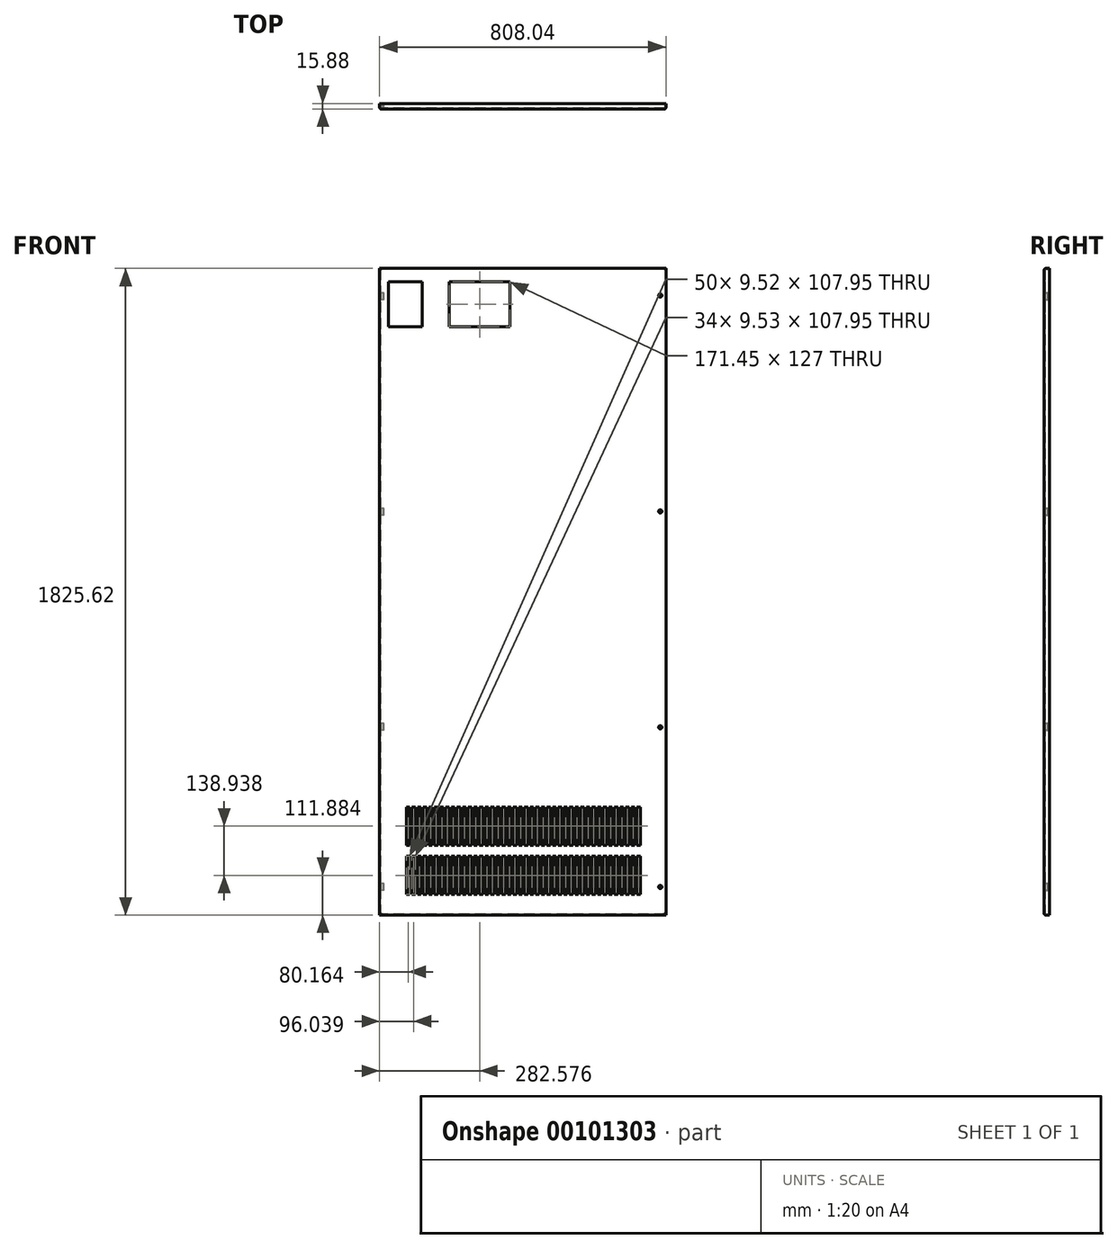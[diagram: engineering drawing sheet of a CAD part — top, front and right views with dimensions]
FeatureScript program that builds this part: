
annotation { "Feature Type Name" : "Feature", "Feature Type Description" : "" }
export const myFeature = defineFeature(function(context is Context, id is Id, definition is map)
    precondition{}
    {
        {
            var Q0;
            Q0=qCreatedBy(makeId("Front.planeOp"),FACE);
            var sketch = newSketch(context, id + "F0", { "sketchPlane" : qUnion([Q0])});
            skLineSegment(sketch, "E0.bottom", {"start": v(404.02, 912.81) * mm, "end": v(-404.02, 912.81) * mm});
            skLineSegment(sketch, "E0.top", {"start": v(404.02, -912.81) * mm, "end": v(-404.02, -912.81) * mm});
            skLineSegment(sketch, "E0.left", {"start": v(404.02, 912.81) * mm, "end": v(404.02, -912.81) * mm});
            skLineSegment(sketch, "E0.right", {"start": v(-404.02, 912.81) * mm, "end": v(-404.02, -912.81) * mm});
            skPoint(sketch, "E0.middle", {"position": v(0, 0) * mm});
            skSolve(sketch);
        }
        {
            var Q0;
            Q0=makeQuery(id+"F0.imprint","IMPRINT",FACE,{"disambiguationData":[TD([[makeQuery(id+"F0.imprint","IMPRINT",EDGE,{"derivedFrom":sQuery(id+"F0.wireOp",EDGE,"E0.bottom")}),1.0]])]});
            var Q1;
            Q1=qSketchRegion(id+"F0",true);
            extrude(context, id + "F1", {"entities" : qUnion([Q0, Q1]), "endBound" : BoundingType.SYMMETRIC, "depth" : 15.88 * mm});
        }
        {
            var Q0;
            Q0=makeQuery(id+"F1.opExtrude","CAP_FACE",FACE,{"disambiguationData":[OSD([sQuery(id+"F0.wireOp",EDGE,"E0.bottom"),sQuery(id+"F0.wireOp",EDGE,"E0.top"),sQuery(id+"F0.wireOp",EDGE,"E0.left"),sQuery(id+"F0.wireOp",EDGE,"E0.right")])],"isStart":true});
            shell(context, id + "F2", {"entities" : qUnion([Q0]), "thickness" : 2.66 * mm});
        }
        {
            var Q0;
            Q0=makeQuery(id+"F1.opExtrude","CAP_EDGE",EDGE,{"disambiguationData":[OSD([sQuery(id+"F0.wireOp",EDGE,"E0.bottom")])],"isStart":false});
            var Q1;
            Q1=makeQuery(id+"F1.opExtrude","CAP_EDGE",EDGE,{"disambiguationData":[OSD([sQuery(id+"F0.wireOp",EDGE,"E0.left")])],"isStart":false});
            var Q2;
            Q2=makeQuery(id+"F1.opExtrude","CAP_EDGE",EDGE,{"disambiguationData":[OSD([sQuery(id+"F0.wireOp",EDGE,"E0.right")])],"isStart":false});
            var Q3;
            Q3=makeQuery(id+"F1.opExtrude","CAP_EDGE",EDGE,{"disambiguationData":[OSD([sQuery(id+"F0.wireOp",EDGE,"E0.top")])],"isStart":false});
            fillet(context, id + "F3", {"entities" : qUnion([Q0, Q1, Q2, Q3]), "radius" : 5.08 * mm, "tangentPropagation" : true, "allowEdgeOverflow" : false});
        }
        {
            var Q0;
            Q0=makeQuery(id+"F1.opExtrude","CAP_FACE",FACE,{"disambiguationData":[OSD([sQuery(id+"F0.wireOp",EDGE,"E0.bottom"),sQuery(id+"F0.wireOp",EDGE,"E0.top"),sQuery(id+"F0.wireOp",EDGE,"E0.left"),sQuery(id+"F0.wireOp",EDGE,"E0.right")])],"isStart":false});
            var sketch = newSketch(context, id + "F4", { "sketchPlane" : qUnion([Q0])});
            skLineSegment(sketch, "E1.bottom", {"start": v(-378.62, 874.71) * mm, "end": v(-283.37, 874.71) * mm});
            skLineSegment(sketch, "E1.top", {"start": v(-378.62, 747.71) * mm, "end": v(-283.37, 747.71) * mm});
            skLineSegment(sketch, "E1.left", {"start": v(-378.62, 874.71) * mm, "end": v(-378.62, 747.71) * mm});
            skLineSegment(sketch, "E1.right", {"start": v(-283.37, 874.71) * mm, "end": v(-283.37, 747.71) * mm});
            skCircle(sketch, "E2", {"center": v(388.14, 836.61) * mm, "radius": 4.76 * mm});
            skCircle(sketch, "E3", {"center": v(388.14, -382.59) * mm, "radius": 4.76 * mm});
            skCircle(sketch, "E4", {"center": v(388.14, -833.44) * mm, "radius": 4.76 * mm});
            skLineSegment(sketch, "E5.bottom", {"start": v(322.26, -854.9) * mm, "end": v(331.78, -854.9) * mm});
            skLineSegment(sketch, "E5.top", {"start": v(322.26, -746.95) * mm, "end": v(331.78, -746.95) * mm});
            skLineSegment(sketch, "E5.left", {"start": v(322.26, -854.9) * mm, "end": v(322.26, -746.95) * mm});
            skLineSegment(sketch, "E5.right", {"start": v(331.78, -854.9) * mm, "end": v(331.78, -746.95) * mm});
            skLineSegment(sketch, "E6.1.0.0", {"start": v(315.9, -854.9) * mm, "end": v(315.9, -746.95) * mm});
            skLineSegment(sketch, "E6.1.0.1", {"start": v(306.38, -854.9) * mm, "end": v(306.38, -746.95) * mm});
            skLineSegment(sketch, "E6.1.0.2", {"start": v(306.38, -854.9) * mm, "end": v(315.9, -854.9) * mm});
            skLineSegment(sketch, "E6.1.0.3", {"start": v(306.38, -746.95) * mm, "end": v(315.9, -746.95) * mm});
            skLineSegment(sketch, "E6.2.0.0", {"start": v(300.03, -854.9) * mm, "end": v(300.03, -746.95) * mm});
            skLineSegment(sketch, "E6.2.0.1", {"start": v(290.5, -854.9) * mm, "end": v(290.5, -746.95) * mm});
            skLineSegment(sketch, "E6.2.0.2", {"start": v(290.5, -854.9) * mm, "end": v(300.03, -854.9) * mm});
            skLineSegment(sketch, "E6.2.0.3", {"start": v(290.5, -746.95) * mm, "end": v(300.03, -746.95) * mm});
            skLineSegment(sketch, "E6.3.0.0", {"start": v(284.16, -854.9) * mm, "end": v(284.16, -746.95) * mm});
            skLineSegment(sketch, "E6.3.0.1", {"start": v(274.63, -854.9) * mm, "end": v(274.63, -746.95) * mm});
            skLineSegment(sketch, "E6.3.0.2", {"start": v(274.63, -854.9) * mm, "end": v(284.16, -854.9) * mm});
            skLineSegment(sketch, "E6.3.0.3", {"start": v(274.63, -746.95) * mm, "end": v(284.16, -746.95) * mm});
            skLineSegment(sketch, "E6.4.0.0", {"start": v(268.28, -854.9) * mm, "end": v(268.28, -746.95) * mm});
            skLineSegment(sketch, "E6.4.0.1", {"start": v(258.76, -854.9) * mm, "end": v(258.76, -746.95) * mm});
            skLineSegment(sketch, "E6.4.0.2", {"start": v(258.76, -854.9) * mm, "end": v(268.28, -854.9) * mm});
            skLineSegment(sketch, "E6.4.0.3", {"start": v(258.76, -746.95) * mm, "end": v(268.28, -746.95) * mm});
            skLineSegment(sketch, "E6.5.0.0", {"start": v(252.4, -854.9) * mm, "end": v(252.4, -746.95) * mm});
            skLineSegment(sketch, "E6.5.0.1", {"start": v(242.88, -854.9) * mm, "end": v(242.88, -746.95) * mm});
            skLineSegment(sketch, "E6.5.0.2", {"start": v(242.88, -854.9) * mm, "end": v(252.4, -854.9) * mm});
            skLineSegment(sketch, "E6.5.0.3", {"start": v(242.88, -746.95) * mm, "end": v(252.4, -746.95) * mm});
            skLineSegment(sketch, "E6.6.0.0", {"start": v(236.53, -854.9) * mm, "end": v(236.53, -746.95) * mm});
            skLineSegment(sketch, "E6.6.0.1", {"start": v(227, -854.9) * mm, "end": v(227, -746.95) * mm});
            skLineSegment(sketch, "E6.6.0.2", {"start": v(227, -854.9) * mm, "end": v(236.53, -854.9) * mm});
            skLineSegment(sketch, "E6.6.0.3", {"start": v(227, -746.95) * mm, "end": v(236.53, -746.95) * mm});
            skLineSegment(sketch, "E6.7.0.0", {"start": v(220.66, -854.9) * mm, "end": v(220.66, -746.95) * mm});
            skLineSegment(sketch, "E6.7.0.1", {"start": v(211.13, -854.9) * mm, "end": v(211.13, -746.95) * mm});
            skLineSegment(sketch, "E6.7.0.2", {"start": v(211.13, -854.9) * mm, "end": v(220.66, -854.9) * mm});
            skLineSegment(sketch, "E6.7.0.3", {"start": v(211.13, -746.95) * mm, "end": v(220.66, -746.95) * mm});
            skLineSegment(sketch, "E6.8.0.0", {"start": v(204.78, -854.9) * mm, "end": v(204.78, -746.95) * mm});
            skLineSegment(sketch, "E6.8.0.1", {"start": v(195.26, -854.9) * mm, "end": v(195.26, -746.95) * mm});
            skLineSegment(sketch, "E6.8.0.2", {"start": v(195.26, -854.9) * mm, "end": v(204.78, -854.9) * mm});
            skLineSegment(sketch, "E6.8.0.3", {"start": v(195.26, -746.95) * mm, "end": v(204.78, -746.95) * mm});
            skLineSegment(sketch, "E6.9.0.0", {"start": v(188.9, -854.9) * mm, "end": v(188.9, -746.95) * mm});
            skLineSegment(sketch, "E6.9.0.1", {"start": v(179.38, -854.9) * mm, "end": v(179.38, -746.95) * mm});
            skLineSegment(sketch, "E6.9.0.2", {"start": v(179.38, -854.9) * mm, "end": v(188.9, -854.9) * mm});
            skLineSegment(sketch, "E6.9.0.3", {"start": v(179.38, -746.95) * mm, "end": v(188.9, -746.95) * mm});
            skLineSegment(sketch, "E6.10.0.0", {"start": v(173.03, -854.9) * mm, "end": v(173.03, -746.95) * mm});
            skLineSegment(sketch, "E6.10.0.1", {"start": v(163.5, -854.9) * mm, "end": v(163.5, -746.95) * mm});
            skLineSegment(sketch, "E6.10.0.2", {"start": v(163.5, -854.9) * mm, "end": v(173.03, -854.9) * mm});
            skLineSegment(sketch, "E6.10.0.3", {"start": v(163.5, -746.95) * mm, "end": v(173.03, -746.95) * mm});
            skLineSegment(sketch, "E6.11.0.0", {"start": v(157.16, -854.9) * mm, "end": v(157.16, -746.95) * mm});
            skLineSegment(sketch, "E6.11.0.1", {"start": v(147.63, -854.9) * mm, "end": v(147.63, -746.95) * mm});
            skLineSegment(sketch, "E6.11.0.2", {"start": v(147.63, -854.9) * mm, "end": v(157.16, -854.9) * mm});
            skLineSegment(sketch, "E6.11.0.3", {"start": v(147.63, -746.95) * mm, "end": v(157.16, -746.95) * mm});
            skLineSegment(sketch, "E6.12.0.0", {"start": v(141.28, -854.9) * mm, "end": v(141.28, -746.95) * mm});
            skLineSegment(sketch, "E6.12.0.1", {"start": v(131.76, -854.9) * mm, "end": v(131.76, -746.95) * mm});
            skLineSegment(sketch, "E6.12.0.2", {"start": v(131.76, -854.9) * mm, "end": v(141.28, -854.9) * mm});
            skLineSegment(sketch, "E6.12.0.3", {"start": v(131.76, -746.95) * mm, "end": v(141.28, -746.95) * mm});
            skLineSegment(sketch, "E6.13.0.0", {"start": v(125.4, -854.9) * mm, "end": v(125.4, -746.95) * mm});
            skLineSegment(sketch, "E6.13.0.1", {"start": v(115.88, -854.9) * mm, "end": v(115.88, -746.95) * mm});
            skLineSegment(sketch, "E6.13.0.2", {"start": v(115.88, -854.9) * mm, "end": v(125.4, -854.9) * mm});
            skLineSegment(sketch, "E6.13.0.3", {"start": v(115.88, -746.95) * mm, "end": v(125.4, -746.95) * mm});
            skLineSegment(sketch, "E6.14.0.0", {"start": v(109.53, -854.9) * mm, "end": v(109.53, -746.95) * mm});
            skLineSegment(sketch, "E6.14.0.1", {"start": v(100, -854.9) * mm, "end": v(100, -746.95) * mm});
            skLineSegment(sketch, "E6.14.0.2", {"start": v(100, -854.9) * mm, "end": v(109.53, -854.9) * mm});
            skLineSegment(sketch, "E6.14.0.3", {"start": v(100, -746.95) * mm, "end": v(109.53, -746.95) * mm});
            skLineSegment(sketch, "E6.15.0.0", {"start": v(93.66, -854.9) * mm, "end": v(93.66, -746.95) * mm});
            skLineSegment(sketch, "E6.15.0.1", {"start": v(84.13, -854.9) * mm, "end": v(84.13, -746.95) * mm});
            skLineSegment(sketch, "E6.15.0.2", {"start": v(84.13, -854.9) * mm, "end": v(93.66, -854.9) * mm});
            skLineSegment(sketch, "E6.15.0.3", {"start": v(84.13, -746.95) * mm, "end": v(93.66, -746.95) * mm});
            skLineSegment(sketch, "E6.16.0.0", {"start": v(77.78, -854.9) * mm, "end": v(77.78, -746.95) * mm});
            skLineSegment(sketch, "E6.16.0.1", {"start": v(68.26, -854.9) * mm, "end": v(68.26, -746.95) * mm});
            skLineSegment(sketch, "E6.16.0.2", {"start": v(68.26, -854.9) * mm, "end": v(77.78, -854.9) * mm});
            skLineSegment(sketch, "E6.16.0.3", {"start": v(68.26, -746.95) * mm, "end": v(77.78, -746.95) * mm});
            skLineSegment(sketch, "E6.17.0.0", {"start": v(61.9, -854.9) * mm, "end": v(61.9, -746.95) * mm});
            skLineSegment(sketch, "E6.17.0.1", {"start": v(52.38, -854.9) * mm, "end": v(52.38, -746.95) * mm});
            skLineSegment(sketch, "E6.17.0.2", {"start": v(52.38, -854.9) * mm, "end": v(61.9, -854.9) * mm});
            skLineSegment(sketch, "E6.17.0.3", {"start": v(52.38, -746.95) * mm, "end": v(61.9, -746.95) * mm});
            skLineSegment(sketch, "E6.18.0.0", {"start": v(46.03, -854.9) * mm, "end": v(46.03, -746.95) * mm});
            skLineSegment(sketch, "E6.18.0.1", {"start": v(36.5, -854.9) * mm, "end": v(36.5, -746.95) * mm});
            skLineSegment(sketch, "E6.18.0.2", {"start": v(36.5, -854.9) * mm, "end": v(46.03, -854.9) * mm});
            skLineSegment(sketch, "E6.18.0.3", {"start": v(36.5, -746.95) * mm, "end": v(46.03, -746.95) * mm});
            skLineSegment(sketch, "E6.19.0.0", {"start": v(30.16, -854.9) * mm, "end": v(30.16, -746.95) * mm});
            skLineSegment(sketch, "E6.19.0.1", {"start": v(20.63, -854.9) * mm, "end": v(20.63, -746.95) * mm});
            skLineSegment(sketch, "E6.19.0.2", {"start": v(20.63, -854.9) * mm, "end": v(30.16, -854.9) * mm});
            skLineSegment(sketch, "E6.19.0.3", {"start": v(20.63, -746.95) * mm, "end": v(30.16, -746.95) * mm});
            skLineSegment(sketch, "E6.20.0.0", {"start": v(14.28, -854.9) * mm, "end": v(14.28, -746.95) * mm});
            skLineSegment(sketch, "E6.20.0.1", {"start": v(4.76, -854.9) * mm, "end": v(4.76, -746.95) * mm});
            skLineSegment(sketch, "E6.20.0.2", {"start": v(4.76, -854.9) * mm, "end": v(14.28, -854.9) * mm});
            skLineSegment(sketch, "E6.20.0.3", {"start": v(4.76, -746.95) * mm, "end": v(14.28, -746.95) * mm});
            skLineSegment(sketch, "E6.21.0.0", {"start": v(-1.6, -854.9) * mm, "end": v(-1.6, -746.95) * mm});
            skLineSegment(sketch, "E6.21.0.1", {"start": v(-11.12, -854.9) * mm, "end": v(-11.12, -746.95) * mm});
            skLineSegment(sketch, "E6.21.0.2", {"start": v(-11.12, -854.9) * mm, "end": v(-1.6, -854.9) * mm});
            skLineSegment(sketch, "E6.21.0.3", {"start": v(-11.12, -746.95) * mm, "end": v(-1.6, -746.95) * mm});
            skLineSegment(sketch, "E6.22.0.0", {"start": v(-17.47, -854.9) * mm, "end": v(-17.47, -746.95) * mm});
            skLineSegment(sketch, "E6.22.0.1", {"start": v(-27, -854.9) * mm, "end": v(-27, -746.95) * mm});
            skLineSegment(sketch, "E6.22.0.2", {"start": v(-27, -854.9) * mm, "end": v(-17.47, -854.9) * mm});
            skLineSegment(sketch, "E6.22.0.3", {"start": v(-27, -746.95) * mm, "end": v(-17.47, -746.95) * mm});
            skLineSegment(sketch, "E6.23.0.0", {"start": v(-33.34, -854.9) * mm, "end": v(-33.34, -746.95) * mm});
            skLineSegment(sketch, "E6.23.0.1", {"start": v(-42.87, -854.9) * mm, "end": v(-42.87, -746.95) * mm});
            skLineSegment(sketch, "E6.23.0.2", {"start": v(-42.87, -854.9) * mm, "end": v(-33.34, -854.9) * mm});
            skLineSegment(sketch, "E6.23.0.3", {"start": v(-42.87, -746.95) * mm, "end": v(-33.34, -746.95) * mm});
            skLineSegment(sketch, "E6.24.0.0", {"start": v(-49.22, -854.9) * mm, "end": v(-49.22, -746.95) * mm});
            skLineSegment(sketch, "E6.24.0.1", {"start": v(-58.74, -854.9) * mm, "end": v(-58.74, -746.95) * mm});
            skLineSegment(sketch, "E6.24.0.2", {"start": v(-58.74, -854.9) * mm, "end": v(-49.22, -854.9) * mm});
            skLineSegment(sketch, "E6.24.0.3", {"start": v(-58.74, -746.95) * mm, "end": v(-49.22, -746.95) * mm});
            skLineSegment(sketch, "E6.25.0.0", {"start": v(-65.1, -854.9) * mm, "end": v(-65.1, -746.95) * mm});
            skLineSegment(sketch, "E6.25.0.1", {"start": v(-74.62, -854.9) * mm, "end": v(-74.62, -746.95) * mm});
            skLineSegment(sketch, "E6.25.0.2", {"start": v(-74.62, -854.9) * mm, "end": v(-65.1, -854.9) * mm});
            skLineSegment(sketch, "E6.25.0.3", {"start": v(-74.62, -746.95) * mm, "end": v(-65.1, -746.95) * mm});
            skLineSegment(sketch, "E6.26.0.0", {"start": v(-80.97, -854.9) * mm, "end": v(-80.97, -746.95) * mm});
            skLineSegment(sketch, "E6.26.0.1", {"start": v(-90.5, -854.9) * mm, "end": v(-90.5, -746.95) * mm});
            skLineSegment(sketch, "E6.26.0.2", {"start": v(-90.5, -854.9) * mm, "end": v(-80.97, -854.9) * mm});
            skLineSegment(sketch, "E6.26.0.3", {"start": v(-90.5, -746.95) * mm, "end": v(-80.97, -746.95) * mm});
            skLineSegment(sketch, "E6.27.0.0", {"start": v(-96.84, -854.9) * mm, "end": v(-96.84, -746.95) * mm});
            skLineSegment(sketch, "E6.27.0.1", {"start": v(-106.37, -854.9) * mm, "end": v(-106.37, -746.95) * mm});
            skLineSegment(sketch, "E6.27.0.2", {"start": v(-106.37, -854.9) * mm, "end": v(-96.84, -854.9) * mm});
            skLineSegment(sketch, "E6.27.0.3", {"start": v(-106.37, -746.95) * mm, "end": v(-96.84, -746.95) * mm});
            skLineSegment(sketch, "E6.28.0.0", {"start": v(-112.72, -854.9) * mm, "end": v(-112.72, -746.95) * mm});
            skLineSegment(sketch, "E6.28.0.1", {"start": v(-122.24, -854.9) * mm, "end": v(-122.24, -746.95) * mm});
            skLineSegment(sketch, "E6.28.0.2", {"start": v(-122.24, -854.9) * mm, "end": v(-112.72, -854.9) * mm});
            skLineSegment(sketch, "E6.28.0.3", {"start": v(-122.24, -746.95) * mm, "end": v(-112.72, -746.95) * mm});
            skLineSegment(sketch, "E6.29.0.0", {"start": v(-128.6, -854.9) * mm, "end": v(-128.6, -746.95) * mm});
            skLineSegment(sketch, "E6.29.0.1", {"start": v(-138.12, -854.9) * mm, "end": v(-138.12, -746.95) * mm});
            skLineSegment(sketch, "E6.29.0.2", {"start": v(-138.12, -854.9) * mm, "end": v(-128.6, -854.9) * mm});
            skLineSegment(sketch, "E6.29.0.3", {"start": v(-138.12, -746.95) * mm, "end": v(-128.6, -746.95) * mm});
            skLineSegment(sketch, "E6.30.0.0", {"start": v(-144.47, -854.9) * mm, "end": v(-144.47, -746.95) * mm});
            skLineSegment(sketch, "E6.30.0.1", {"start": v(-154, -854.9) * mm, "end": v(-154, -746.95) * mm});
            skLineSegment(sketch, "E6.30.0.2", {"start": v(-154, -854.9) * mm, "end": v(-144.47, -854.9) * mm});
            skLineSegment(sketch, "E6.30.0.3", {"start": v(-154, -746.95) * mm, "end": v(-144.47, -746.95) * mm});
            skLineSegment(sketch, "E6.31.0.0", {"start": v(-160.34, -854.9) * mm, "end": v(-160.34, -746.95) * mm});
            skLineSegment(sketch, "E6.31.0.1", {"start": v(-169.87, -854.9) * mm, "end": v(-169.87, -746.95) * mm});
            skLineSegment(sketch, "E6.31.0.2", {"start": v(-169.87, -854.9) * mm, "end": v(-160.34, -854.9) * mm});
            skLineSegment(sketch, "E6.31.0.3", {"start": v(-169.87, -746.95) * mm, "end": v(-160.34, -746.95) * mm});
            skLineSegment(sketch, "E6.32.0.0", {"start": v(-176.22, -854.9) * mm, "end": v(-176.22, -746.95) * mm});
            skLineSegment(sketch, "E6.32.0.1", {"start": v(-185.74, -854.9) * mm, "end": v(-185.74, -746.95) * mm});
            skLineSegment(sketch, "E6.32.0.2", {"start": v(-185.74, -854.9) * mm, "end": v(-176.22, -854.9) * mm});
            skLineSegment(sketch, "E6.32.0.3", {"start": v(-185.74, -746.95) * mm, "end": v(-176.22, -746.95) * mm});
            skLineSegment(sketch, "E6.33.0.0", {"start": v(-192.1, -854.9) * mm, "end": v(-192.1, -746.95) * mm});
            skLineSegment(sketch, "E6.33.0.1", {"start": v(-201.62, -854.9) * mm, "end": v(-201.62, -746.95) * mm});
            skLineSegment(sketch, "E6.33.0.2", {"start": v(-201.62, -854.9) * mm, "end": v(-192.1, -854.9) * mm});
            skLineSegment(sketch, "E6.33.0.3", {"start": v(-201.62, -746.95) * mm, "end": v(-192.1, -746.95) * mm});
            skLineSegment(sketch, "E6.direction1", {"start": v(331.78, -854.9) * mm, "end": v(315.9, -854.9) * mm, "construction": true});
            skLineSegment(sketch, "E6.direction2", {"start": v(331.78, -854.9) * mm, "end": v(331.78, -715.96) * mm, "construction": true});
            skLineSegment(sketch, "E7.0.34.0", {"start": v(-207.97, -854.9) * mm, "end": v(-207.97, -746.95) * mm});
            skLineSegment(sketch, "E7.3.34.0", {"start": v(-217.5, -854.9) * mm, "end": v(-217.5, -746.95) * mm});
            skLineSegment(sketch, "E7.6.34.0", {"start": v(-217.5, -854.9) * mm, "end": v(-207.97, -854.9) * mm});
            skLineSegment(sketch, "E7.9.34.0", {"start": v(-217.5, -746.95) * mm, "end": v(-207.97, -746.95) * mm});
            skLineSegment(sketch, "E7.0.35.0", {"start": v(-223.84, -854.9) * mm, "end": v(-223.84, -746.95) * mm});
            skLineSegment(sketch, "E7.3.35.0", {"start": v(-233.37, -854.9) * mm, "end": v(-233.37, -746.95) * mm});
            skLineSegment(sketch, "E7.6.35.0", {"start": v(-233.37, -854.9) * mm, "end": v(-223.84, -854.9) * mm});
            skLineSegment(sketch, "E7.9.35.0", {"start": v(-233.37, -746.95) * mm, "end": v(-223.84, -746.95) * mm});
            skLineSegment(sketch, "E7.0.36.0", {"start": v(-239.72, -854.9) * mm, "end": v(-239.72, -746.95) * mm});
            skLineSegment(sketch, "E7.3.36.0", {"start": v(-249.24, -854.9) * mm, "end": v(-249.24, -746.95) * mm});
            skLineSegment(sketch, "E7.6.36.0", {"start": v(-249.24, -854.9) * mm, "end": v(-239.72, -854.9) * mm});
            skLineSegment(sketch, "E7.9.36.0", {"start": v(-249.24, -746.95) * mm, "end": v(-239.72, -746.95) * mm});
            skLineSegment(sketch, "E7.0.37.0", {"start": v(-255.6, -854.9) * mm, "end": v(-255.6, -746.95) * mm});
            skLineSegment(sketch, "E7.3.37.0", {"start": v(-265.12, -854.9) * mm, "end": v(-265.12, -746.95) * mm});
            skLineSegment(sketch, "E7.6.37.0", {"start": v(-265.12, -854.9) * mm, "end": v(-255.6, -854.9) * mm});
            skLineSegment(sketch, "E7.9.37.0", {"start": v(-265.12, -746.95) * mm, "end": v(-255.6, -746.95) * mm});
            skLineSegment(sketch, "E7.0.38.0", {"start": v(-271.47, -854.9) * mm, "end": v(-271.47, -746.95) * mm});
            skLineSegment(sketch, "E7.3.38.0", {"start": v(-281, -854.9) * mm, "end": v(-281, -746.95) * mm});
            skLineSegment(sketch, "E7.6.38.0", {"start": v(-281, -854.9) * mm, "end": v(-271.47, -854.9) * mm});
            skLineSegment(sketch, "E7.9.38.0", {"start": v(-281, -746.95) * mm, "end": v(-271.47, -746.95) * mm});
            skLineSegment(sketch, "E7.0.39.0", {"start": v(-287.34, -854.9) * mm, "end": v(-287.34, -746.95) * mm});
            skLineSegment(sketch, "E7.3.39.0", {"start": v(-296.87, -854.9) * mm, "end": v(-296.87, -746.95) * mm});
            skLineSegment(sketch, "E7.6.39.0", {"start": v(-296.87, -854.9) * mm, "end": v(-287.34, -854.9) * mm});
            skLineSegment(sketch, "E7.9.39.0", {"start": v(-296.87, -746.95) * mm, "end": v(-287.34, -746.95) * mm});
            skLineSegment(sketch, "E7.0.40.0", {"start": v(-303.22, -854.9) * mm, "end": v(-303.22, -746.95) * mm});
            skLineSegment(sketch, "E7.3.40.0", {"start": v(-312.74, -854.9) * mm, "end": v(-312.74, -746.95) * mm});
            skLineSegment(sketch, "E7.6.40.0", {"start": v(-312.74, -854.9) * mm, "end": v(-303.22, -854.9) * mm});
            skLineSegment(sketch, "E7.9.40.0", {"start": v(-312.74, -746.95) * mm, "end": v(-303.22, -746.95) * mm});
            skLineSegment(sketch, "E7.0.41.0", {"start": v(-319.1, -854.9) * mm, "end": v(-319.1, -746.95) * mm});
            skLineSegment(sketch, "E7.3.41.0", {"start": v(-328.62, -854.9) * mm, "end": v(-328.62, -746.95) * mm});
            skLineSegment(sketch, "E7.6.41.0", {"start": v(-328.62, -854.9) * mm, "end": v(-319.1, -854.9) * mm});
            skLineSegment(sketch, "E7.9.41.0", {"start": v(-328.62, -746.95) * mm, "end": v(-319.1, -746.95) * mm});
            skLineSegment(sketch, "E8.direction1", {"start": v(-281, -854.9) * mm, "end": v(-259.44, -854.9) * mm, "construction": true});
            skLineSegment(sketch, "E9.0.0.1", {"start": v(331.78, -715.96) * mm, "end": v(331.78, -608.01) * mm});
            skLineSegment(sketch, "E9.3.0.1", {"start": v(322.26, -715.96) * mm, "end": v(322.26, -608.01) * mm});
            skLineSegment(sketch, "E9.6.0.1", {"start": v(322.26, -715.96) * mm, "end": v(331.78, -715.96) * mm});
            skLineSegment(sketch, "E9.9.0.1", {"start": v(322.26, -608.01) * mm, "end": v(331.78, -608.01) * mm});
            skLineSegment(sketch, "E9.0.1.1", {"start": v(315.9, -715.96) * mm, "end": v(315.9, -608.01) * mm});
            skLineSegment(sketch, "E9.3.1.1", {"start": v(306.38, -715.96) * mm, "end": v(306.38, -608.01) * mm});
            skLineSegment(sketch, "E9.6.1.1", {"start": v(306.38, -715.96) * mm, "end": v(315.9, -715.96) * mm});
            skLineSegment(sketch, "E9.9.1.1", {"start": v(306.38, -608.01) * mm, "end": v(315.9, -608.01) * mm});
            skLineSegment(sketch, "E9.0.2.1", {"start": v(300.03, -715.96) * mm, "end": v(300.03, -608.01) * mm});
            skLineSegment(sketch, "E9.3.2.1", {"start": v(290.5, -715.96) * mm, "end": v(290.5, -608.01) * mm});
            skLineSegment(sketch, "E9.6.2.1", {"start": v(290.5, -715.96) * mm, "end": v(300.03, -715.96) * mm});
            skLineSegment(sketch, "E9.9.2.1", {"start": v(290.5, -608.01) * mm, "end": v(300.03, -608.01) * mm});
            skLineSegment(sketch, "E9.0.3.1", {"start": v(284.16, -715.96) * mm, "end": v(284.16, -608.01) * mm});
            skLineSegment(sketch, "E9.3.3.1", {"start": v(274.63, -715.96) * mm, "end": v(274.63, -608.01) * mm});
            skLineSegment(sketch, "E9.6.3.1", {"start": v(274.63, -715.96) * mm, "end": v(284.16, -715.96) * mm});
            skLineSegment(sketch, "E9.9.3.1", {"start": v(274.63, -608.01) * mm, "end": v(284.16, -608.01) * mm});
            skLineSegment(sketch, "E9.0.4.1", {"start": v(268.28, -715.96) * mm, "end": v(268.28, -608.01) * mm});
            skLineSegment(sketch, "E9.3.4.1", {"start": v(258.76, -715.96) * mm, "end": v(258.76, -608.01) * mm});
            skLineSegment(sketch, "E9.6.4.1", {"start": v(258.76, -715.96) * mm, "end": v(268.28, -715.96) * mm});
            skLineSegment(sketch, "E9.9.4.1", {"start": v(258.76, -608.01) * mm, "end": v(268.28, -608.01) * mm});
            skLineSegment(sketch, "E9.0.5.1", {"start": v(252.4, -715.96) * mm, "end": v(252.4, -608.01) * mm});
            skLineSegment(sketch, "E9.3.5.1", {"start": v(242.88, -715.96) * mm, "end": v(242.88, -608.01) * mm});
            skLineSegment(sketch, "E9.6.5.1", {"start": v(242.88, -715.96) * mm, "end": v(252.4, -715.96) * mm});
            skLineSegment(sketch, "E9.9.5.1", {"start": v(242.88, -608.01) * mm, "end": v(252.4, -608.01) * mm});
            skLineSegment(sketch, "E9.0.6.1", {"start": v(236.53, -715.96) * mm, "end": v(236.53, -608.01) * mm});
            skLineSegment(sketch, "E9.3.6.1", {"start": v(227, -715.96) * mm, "end": v(227, -608.01) * mm});
            skLineSegment(sketch, "E9.6.6.1", {"start": v(227, -715.96) * mm, "end": v(236.53, -715.96) * mm});
            skLineSegment(sketch, "E9.9.6.1", {"start": v(227, -608.01) * mm, "end": v(236.53, -608.01) * mm});
            skLineSegment(sketch, "E9.0.7.1", {"start": v(220.66, -715.96) * mm, "end": v(220.66, -608.01) * mm});
            skLineSegment(sketch, "E9.3.7.1", {"start": v(211.13, -715.96) * mm, "end": v(211.13, -608.01) * mm});
            skLineSegment(sketch, "E9.6.7.1", {"start": v(211.13, -715.96) * mm, "end": v(220.66, -715.96) * mm});
            skLineSegment(sketch, "E9.9.7.1", {"start": v(211.13, -608.01) * mm, "end": v(220.66, -608.01) * mm});
            skLineSegment(sketch, "E9.0.8.1", {"start": v(204.78, -715.96) * mm, "end": v(204.78, -608.01) * mm});
            skLineSegment(sketch, "E9.3.8.1", {"start": v(195.26, -715.96) * mm, "end": v(195.26, -608.01) * mm});
            skLineSegment(sketch, "E9.6.8.1", {"start": v(195.26, -715.96) * mm, "end": v(204.78, -715.96) * mm});
            skLineSegment(sketch, "E9.9.8.1", {"start": v(195.26, -608.01) * mm, "end": v(204.78, -608.01) * mm});
            skLineSegment(sketch, "E9.0.9.1", {"start": v(188.9, -715.96) * mm, "end": v(188.9, -608.01) * mm});
            skLineSegment(sketch, "E9.3.9.1", {"start": v(179.38, -715.96) * mm, "end": v(179.38, -608.01) * mm});
            skLineSegment(sketch, "E9.6.9.1", {"start": v(179.38, -715.96) * mm, "end": v(188.9, -715.96) * mm});
            skLineSegment(sketch, "E9.9.9.1", {"start": v(179.38, -608.01) * mm, "end": v(188.9, -608.01) * mm});
            skLineSegment(sketch, "E9.0.10.1", {"start": v(173.03, -715.96) * mm, "end": v(173.03, -608.01) * mm});
            skLineSegment(sketch, "E9.3.10.1", {"start": v(163.5, -715.96) * mm, "end": v(163.5, -608.01) * mm});
            skLineSegment(sketch, "E9.6.10.1", {"start": v(163.5, -715.96) * mm, "end": v(173.03, -715.96) * mm});
            skLineSegment(sketch, "E9.9.10.1", {"start": v(163.5, -608.01) * mm, "end": v(173.03, -608.01) * mm});
            skLineSegment(sketch, "E9.0.11.1", {"start": v(157.16, -715.96) * mm, "end": v(157.16, -608.01) * mm});
            skLineSegment(sketch, "E9.3.11.1", {"start": v(147.63, -715.96) * mm, "end": v(147.63, -608.01) * mm});
            skLineSegment(sketch, "E9.6.11.1", {"start": v(147.63, -715.96) * mm, "end": v(157.16, -715.96) * mm});
            skLineSegment(sketch, "E9.9.11.1", {"start": v(147.63, -608.01) * mm, "end": v(157.16, -608.01) * mm});
            skLineSegment(sketch, "E9.0.12.1", {"start": v(141.28, -715.96) * mm, "end": v(141.28, -608.01) * mm});
            skLineSegment(sketch, "E9.3.12.1", {"start": v(131.76, -715.96) * mm, "end": v(131.76, -608.01) * mm});
            skLineSegment(sketch, "E9.6.12.1", {"start": v(131.76, -715.96) * mm, "end": v(141.28, -715.96) * mm});
            skLineSegment(sketch, "E9.9.12.1", {"start": v(131.76, -608.01) * mm, "end": v(141.28, -608.01) * mm});
            skLineSegment(sketch, "E9.0.13.1", {"start": v(125.4, -715.96) * mm, "end": v(125.4, -608.01) * mm});
            skLineSegment(sketch, "E9.3.13.1", {"start": v(115.88, -715.96) * mm, "end": v(115.88, -608.01) * mm});
            skLineSegment(sketch, "E9.6.13.1", {"start": v(115.88, -715.96) * mm, "end": v(125.4, -715.96) * mm});
            skLineSegment(sketch, "E9.9.13.1", {"start": v(115.88, -608.01) * mm, "end": v(125.4, -608.01) * mm});
            skLineSegment(sketch, "E9.0.14.1", {"start": v(109.53, -715.96) * mm, "end": v(109.53, -608.01) * mm});
            skLineSegment(sketch, "E9.3.14.1", {"start": v(100, -715.96) * mm, "end": v(100, -608.01) * mm});
            skLineSegment(sketch, "E9.6.14.1", {"start": v(100, -715.96) * mm, "end": v(109.53, -715.96) * mm});
            skLineSegment(sketch, "E9.9.14.1", {"start": v(100, -608.01) * mm, "end": v(109.53, -608.01) * mm});
            skLineSegment(sketch, "E9.0.15.1", {"start": v(93.66, -715.96) * mm, "end": v(93.66, -608.01) * mm});
            skLineSegment(sketch, "E9.3.15.1", {"start": v(84.13, -715.96) * mm, "end": v(84.13, -608.01) * mm});
            skLineSegment(sketch, "E9.6.15.1", {"start": v(84.13, -715.96) * mm, "end": v(93.66, -715.96) * mm});
            skLineSegment(sketch, "E9.9.15.1", {"start": v(84.13, -608.01) * mm, "end": v(93.66, -608.01) * mm});
            skLineSegment(sketch, "E9.0.16.1", {"start": v(77.78, -715.96) * mm, "end": v(77.78, -608.01) * mm});
            skLineSegment(sketch, "E9.3.16.1", {"start": v(68.26, -715.96) * mm, "end": v(68.26, -608.01) * mm});
            skLineSegment(sketch, "E9.6.16.1", {"start": v(68.26, -715.96) * mm, "end": v(77.78, -715.96) * mm});
            skLineSegment(sketch, "E9.9.16.1", {"start": v(68.26, -608.01) * mm, "end": v(77.78, -608.01) * mm});
            skLineSegment(sketch, "E9.0.17.1", {"start": v(61.9, -715.96) * mm, "end": v(61.9, -608.01) * mm});
            skLineSegment(sketch, "E9.3.17.1", {"start": v(52.38, -715.96) * mm, "end": v(52.38, -608.01) * mm});
            skLineSegment(sketch, "E9.6.17.1", {"start": v(52.38, -715.96) * mm, "end": v(61.9, -715.96) * mm});
            skLineSegment(sketch, "E9.9.17.1", {"start": v(52.38, -608.01) * mm, "end": v(61.9, -608.01) * mm});
            skLineSegment(sketch, "E9.0.18.1", {"start": v(46.03, -715.96) * mm, "end": v(46.03, -608.01) * mm});
            skLineSegment(sketch, "E9.3.18.1", {"start": v(36.5, -715.96) * mm, "end": v(36.5, -608.01) * mm});
            skLineSegment(sketch, "E9.6.18.1", {"start": v(36.5, -715.96) * mm, "end": v(46.03, -715.96) * mm});
            skLineSegment(sketch, "E9.9.18.1", {"start": v(36.5, -608.01) * mm, "end": v(46.03, -608.01) * mm});
            skLineSegment(sketch, "E9.0.19.1", {"start": v(30.16, -715.96) * mm, "end": v(30.16, -608.01) * mm});
            skLineSegment(sketch, "E9.3.19.1", {"start": v(20.63, -715.96) * mm, "end": v(20.63, -608.01) * mm});
            skLineSegment(sketch, "E9.6.19.1", {"start": v(20.63, -715.96) * mm, "end": v(30.16, -715.96) * mm});
            skLineSegment(sketch, "E9.9.19.1", {"start": v(20.63, -608.01) * mm, "end": v(30.16, -608.01) * mm});
            skLineSegment(sketch, "E9.0.20.1", {"start": v(14.28, -715.96) * mm, "end": v(14.28, -608.01) * mm});
            skLineSegment(sketch, "E9.3.20.1", {"start": v(4.76, -715.96) * mm, "end": v(4.76, -608.01) * mm});
            skLineSegment(sketch, "E9.6.20.1", {"start": v(4.76, -715.96) * mm, "end": v(14.28, -715.96) * mm});
            skLineSegment(sketch, "E9.9.20.1", {"start": v(4.76, -608.01) * mm, "end": v(14.28, -608.01) * mm});
            skLineSegment(sketch, "E9.0.21.1", {"start": v(-1.6, -715.96) * mm, "end": v(-1.6, -608.01) * mm});
            skLineSegment(sketch, "E9.3.21.1", {"start": v(-11.12, -715.96) * mm, "end": v(-11.12, -608.01) * mm});
            skLineSegment(sketch, "E9.6.21.1", {"start": v(-11.12, -715.96) * mm, "end": v(-1.6, -715.96) * mm});
            skLineSegment(sketch, "E9.9.21.1", {"start": v(-11.12, -608.01) * mm, "end": v(-1.6, -608.01) * mm});
            skLineSegment(sketch, "E9.0.22.1", {"start": v(-17.47, -715.96) * mm, "end": v(-17.47, -608.01) * mm});
            skLineSegment(sketch, "E9.3.22.1", {"start": v(-27, -715.96) * mm, "end": v(-27, -608.01) * mm});
            skLineSegment(sketch, "E9.6.22.1", {"start": v(-27, -715.96) * mm, "end": v(-17.47, -715.96) * mm});
            skLineSegment(sketch, "E9.9.22.1", {"start": v(-27, -608.01) * mm, "end": v(-17.47, -608.01) * mm});
            skLineSegment(sketch, "E9.0.23.1", {"start": v(-33.34, -715.96) * mm, "end": v(-33.34, -608.01) * mm});
            skLineSegment(sketch, "E9.3.23.1", {"start": v(-42.87, -715.96) * mm, "end": v(-42.87, -608.01) * mm});
            skLineSegment(sketch, "E9.6.23.1", {"start": v(-42.87, -715.96) * mm, "end": v(-33.34, -715.96) * mm});
            skLineSegment(sketch, "E9.9.23.1", {"start": v(-42.87, -608.01) * mm, "end": v(-33.34, -608.01) * mm});
            skLineSegment(sketch, "E9.0.24.1", {"start": v(-49.22, -715.96) * mm, "end": v(-49.22, -608.01) * mm});
            skLineSegment(sketch, "E9.3.24.1", {"start": v(-58.74, -715.96) * mm, "end": v(-58.74, -608.01) * mm});
            skLineSegment(sketch, "E9.6.24.1", {"start": v(-58.74, -715.96) * mm, "end": v(-49.22, -715.96) * mm});
            skLineSegment(sketch, "E9.9.24.1", {"start": v(-58.74, -608.01) * mm, "end": v(-49.22, -608.01) * mm});
            skLineSegment(sketch, "E9.0.25.1", {"start": v(-65.1, -715.96) * mm, "end": v(-65.1, -608.01) * mm});
            skLineSegment(sketch, "E9.3.25.1", {"start": v(-74.62, -715.96) * mm, "end": v(-74.62, -608.01) * mm});
            skLineSegment(sketch, "E9.6.25.1", {"start": v(-74.62, -715.96) * mm, "end": v(-65.1, -715.96) * mm});
            skLineSegment(sketch, "E9.9.25.1", {"start": v(-74.62, -608.01) * mm, "end": v(-65.1, -608.01) * mm});
            skLineSegment(sketch, "E9.0.26.1", {"start": v(-80.97, -715.96) * mm, "end": v(-80.97, -608.01) * mm});
            skLineSegment(sketch, "E9.3.26.1", {"start": v(-90.5, -715.96) * mm, "end": v(-90.5, -608.01) * mm});
            skLineSegment(sketch, "E9.6.26.1", {"start": v(-90.5, -715.96) * mm, "end": v(-80.97, -715.96) * mm});
            skLineSegment(sketch, "E9.9.26.1", {"start": v(-90.5, -608.01) * mm, "end": v(-80.97, -608.01) * mm});
            skLineSegment(sketch, "E9.0.27.1", {"start": v(-96.84, -715.96) * mm, "end": v(-96.84, -608.01) * mm});
            skLineSegment(sketch, "E9.3.27.1", {"start": v(-106.37, -715.96) * mm, "end": v(-106.37, -608.01) * mm});
            skLineSegment(sketch, "E9.6.27.1", {"start": v(-106.37, -715.96) * mm, "end": v(-96.84, -715.96) * mm});
            skLineSegment(sketch, "E9.9.27.1", {"start": v(-106.37, -608.01) * mm, "end": v(-96.84, -608.01) * mm});
            skLineSegment(sketch, "E9.0.28.1", {"start": v(-112.72, -715.96) * mm, "end": v(-112.72, -608.01) * mm});
            skLineSegment(sketch, "E9.3.28.1", {"start": v(-122.24, -715.96) * mm, "end": v(-122.24, -608.01) * mm});
            skLineSegment(sketch, "E9.6.28.1", {"start": v(-122.24, -715.96) * mm, "end": v(-112.72, -715.96) * mm});
            skLineSegment(sketch, "E9.9.28.1", {"start": v(-122.24, -608.01) * mm, "end": v(-112.72, -608.01) * mm});
            skLineSegment(sketch, "E9.0.29.1", {"start": v(-128.6, -715.96) * mm, "end": v(-128.6, -608.01) * mm});
            skLineSegment(sketch, "E9.3.29.1", {"start": v(-138.12, -715.96) * mm, "end": v(-138.12, -608.01) * mm});
            skLineSegment(sketch, "E9.6.29.1", {"start": v(-138.12, -715.96) * mm, "end": v(-128.6, -715.96) * mm});
            skLineSegment(sketch, "E9.9.29.1", {"start": v(-138.12, -608.01) * mm, "end": v(-128.6, -608.01) * mm});
            skLineSegment(sketch, "E9.0.30.1", {"start": v(-144.47, -715.96) * mm, "end": v(-144.47, -608.01) * mm});
            skLineSegment(sketch, "E9.3.30.1", {"start": v(-154, -715.96) * mm, "end": v(-154, -608.01) * mm});
            skLineSegment(sketch, "E9.6.30.1", {"start": v(-154, -715.96) * mm, "end": v(-144.47, -715.96) * mm});
            skLineSegment(sketch, "E9.9.30.1", {"start": v(-154, -608.01) * mm, "end": v(-144.47, -608.01) * mm});
            skLineSegment(sketch, "E9.0.31.1", {"start": v(-160.34, -715.96) * mm, "end": v(-160.34, -608.01) * mm});
            skLineSegment(sketch, "E9.3.31.1", {"start": v(-169.87, -715.96) * mm, "end": v(-169.87, -608.01) * mm});
            skLineSegment(sketch, "E9.6.31.1", {"start": v(-169.87, -715.96) * mm, "end": v(-160.34, -715.96) * mm});
            skLineSegment(sketch, "E9.9.31.1", {"start": v(-169.87, -608.01) * mm, "end": v(-160.34, -608.01) * mm});
            skLineSegment(sketch, "E9.0.32.1", {"start": v(-176.22, -715.96) * mm, "end": v(-176.22, -608.01) * mm});
            skLineSegment(sketch, "E9.3.32.1", {"start": v(-185.74, -715.96) * mm, "end": v(-185.74, -608.01) * mm});
            skLineSegment(sketch, "E9.6.32.1", {"start": v(-185.74, -715.96) * mm, "end": v(-176.22, -715.96) * mm});
            skLineSegment(sketch, "E9.9.32.1", {"start": v(-185.74, -608.01) * mm, "end": v(-176.22, -608.01) * mm});
            skLineSegment(sketch, "E9.0.33.1", {"start": v(-192.1, -715.96) * mm, "end": v(-192.1, -608.01) * mm});
            skLineSegment(sketch, "E9.3.33.1", {"start": v(-201.62, -715.96) * mm, "end": v(-201.62, -608.01) * mm});
            skLineSegment(sketch, "E9.6.33.1", {"start": v(-201.62, -715.96) * mm, "end": v(-192.1, -715.96) * mm});
            skLineSegment(sketch, "E9.9.33.1", {"start": v(-201.62, -608.01) * mm, "end": v(-192.1, -608.01) * mm});
            skLineSegment(sketch, "E9.0.34.1", {"start": v(-207.97, -715.96) * mm, "end": v(-207.97, -608.01) * mm});
            skLineSegment(sketch, "E9.3.34.1", {"start": v(-217.5, -715.96) * mm, "end": v(-217.5, -608.01) * mm});
            skLineSegment(sketch, "E9.6.34.1", {"start": v(-217.5, -715.96) * mm, "end": v(-207.97, -715.96) * mm});
            skLineSegment(sketch, "E9.9.34.1", {"start": v(-217.5, -608.01) * mm, "end": v(-207.97, -608.01) * mm});
            skLineSegment(sketch, "E9.0.35.1", {"start": v(-223.84, -715.96) * mm, "end": v(-223.84, -608.01) * mm});
            skLineSegment(sketch, "E9.3.35.1", {"start": v(-233.37, -715.96) * mm, "end": v(-233.37, -608.01) * mm});
            skLineSegment(sketch, "E9.6.35.1", {"start": v(-233.37, -715.96) * mm, "end": v(-223.84, -715.96) * mm});
            skLineSegment(sketch, "E9.9.35.1", {"start": v(-233.37, -608.01) * mm, "end": v(-223.84, -608.01) * mm});
            skLineSegment(sketch, "E9.0.36.1", {"start": v(-239.72, -715.96) * mm, "end": v(-239.72, -608.01) * mm});
            skLineSegment(sketch, "E9.3.36.1", {"start": v(-249.24, -715.96) * mm, "end": v(-249.24, -608.01) * mm});
            skLineSegment(sketch, "E9.6.36.1", {"start": v(-249.24, -715.96) * mm, "end": v(-239.72, -715.96) * mm});
            skLineSegment(sketch, "E9.9.36.1", {"start": v(-249.24, -608.01) * mm, "end": v(-239.72, -608.01) * mm});
            skLineSegment(sketch, "E9.0.37.1", {"start": v(-255.6, -715.96) * mm, "end": v(-255.6, -608.01) * mm});
            skLineSegment(sketch, "E9.3.37.1", {"start": v(-265.12, -715.96) * mm, "end": v(-265.12, -608.01) * mm});
            skLineSegment(sketch, "E9.6.37.1", {"start": v(-265.12, -715.96) * mm, "end": v(-255.6, -715.96) * mm});
            skLineSegment(sketch, "E9.9.37.1", {"start": v(-265.12, -608.01) * mm, "end": v(-255.6, -608.01) * mm});
            skLineSegment(sketch, "E9.0.38.1", {"start": v(-271.47, -715.96) * mm, "end": v(-271.47, -608.01) * mm});
            skLineSegment(sketch, "E9.3.38.1", {"start": v(-281, -715.96) * mm, "end": v(-281, -608.01) * mm});
            skLineSegment(sketch, "E9.6.38.1", {"start": v(-281, -715.96) * mm, "end": v(-271.47, -715.96) * mm});
            skLineSegment(sketch, "E9.9.38.1", {"start": v(-281, -608.01) * mm, "end": v(-271.47, -608.01) * mm});
            skLineSegment(sketch, "E9.0.39.1", {"start": v(-287.34, -715.96) * mm, "end": v(-287.34, -608.01) * mm});
            skLineSegment(sketch, "E9.3.39.1", {"start": v(-296.87, -715.96) * mm, "end": v(-296.87, -608.01) * mm});
            skLineSegment(sketch, "E9.6.39.1", {"start": v(-296.87, -715.96) * mm, "end": v(-287.34, -715.96) * mm});
            skLineSegment(sketch, "E9.9.39.1", {"start": v(-296.87, -608.01) * mm, "end": v(-287.34, -608.01) * mm});
            skLineSegment(sketch, "E9.0.40.1", {"start": v(-303.22, -715.96) * mm, "end": v(-303.22, -608.01) * mm});
            skLineSegment(sketch, "E9.3.40.1", {"start": v(-312.74, -715.96) * mm, "end": v(-312.74, -608.01) * mm});
            skLineSegment(sketch, "E9.6.40.1", {"start": v(-312.74, -715.96) * mm, "end": v(-303.22, -715.96) * mm});
            skLineSegment(sketch, "E9.9.40.1", {"start": v(-312.74, -608.01) * mm, "end": v(-303.22, -608.01) * mm});
            skLineSegment(sketch, "E9.0.41.1", {"start": v(-319.1, -715.96) * mm, "end": v(-319.1, -608.01) * mm});
            skLineSegment(sketch, "E9.3.41.1", {"start": v(-328.62, -715.96) * mm, "end": v(-328.62, -608.01) * mm});
            skLineSegment(sketch, "E9.6.41.1", {"start": v(-328.62, -715.96) * mm, "end": v(-319.1, -715.96) * mm});
            skLineSegment(sketch, "E9.9.41.1", {"start": v(-328.62, -608.01) * mm, "end": v(-319.1, -608.01) * mm});
            skCircle(sketch, "E10", {"center": v(388.14, 227.01) * mm, "radius": 4.76 * mm});
            skLineSegment(sketch, "E11.bottom", {"start": v(-207.17, 874.71) * mm, "end": v(-35.72, 874.71) * mm});
            skLineSegment(sketch, "E11.top", {"start": v(-207.17, 747.71) * mm, "end": v(-35.72, 747.71) * mm});
            skLineSegment(sketch, "E11.left", {"start": v(-207.17, 874.71) * mm, "end": v(-207.17, 747.71) * mm});
            skLineSegment(sketch, "E11.right", {"start": v(-35.72, 874.71) * mm, "end": v(-35.72, 747.71) * mm});
            skSolve(sketch);
        }
        {
            var Q0;
            Q0=qSketchRegion(id+"F4",true);
            extrude(context, id + "F5", {"entities" : qUnion([Q0]), "operationType" : NewBodyOperationType.REMOVE, "endBound" : BoundingType.THROUGH_ALL, "oppositeDirection" : true, "depth" : 25.4 * mm});
        }
        {
            var Q0;
            {var subQ0=sQuery(id+"F0.wireOp",EDGE,"E0.right");Q0=makeQuery(id+"F2.opShell","OFFSET_FACE",FACE,{"disambiguationData":[OSD([subQ0]),TDD([makeQuery(id+"F1.opExtrude","SWEPT_FACE",FACE,{"disambiguationData":[OSD([subQ0])]})])]});}
            cPlane(context, id + "F6", {"entities" : qUnion([Q0]), "cplaneType" : CPlaneType.OFFSET, "offset" : 4.76 * mm, "width" : 152.4 * mm, "height" : 152.4 * mm});
        }
        {
            var Q0;
            Q0=qCreatedBy(id+"F6.planeOp",FACE);
            var sketch = newSketch(context, id + "F7", { "sketchPlane" : qUnion([Q0])});
            skLineSegment(sketch, "E12", {"start": v(-0.52, 910.16) * mm, "end": v(-0.52, -910.16) * mm, "construction": true});
            skLineSegment(sketch, "E13.bottom", {"start": v(-5.28, 824.43) * mm, "end": v(-3.7, 824.43) * mm});
            skLineSegment(sketch, "E13.top", {"start": v(-5.28, 843.48) * mm, "end": v(-3.7, 843.48) * mm});
            skLineSegment(sketch, "E13.left", {"start": v(-5.28, 824.43) * mm, "end": v(-5.28, 843.48) * mm});
            skLineSegment(sketch, "E13.right", {"start": v(-3.7, 824.43) * mm, "end": v(-3.7, 843.48) * mm});
            skPoint(sketch, "E13.middle", {"position": v(-4.49, 833.96) * mm});
            skLineSegment(sketch, "E14.bottom", {"start": v(-5.28, 216.42) * mm, "end": v(-3.7, 216.42) * mm});
            skLineSegment(sketch, "E14.top", {"start": v(-5.28, 235.47) * mm, "end": v(-3.7, 235.47) * mm});
            skLineSegment(sketch, "E14.left", {"start": v(-5.28, 216.42) * mm, "end": v(-5.28, 235.47) * mm});
            skLineSegment(sketch, "E14.right", {"start": v(-3.7, 216.42) * mm, "end": v(-3.7, 235.47) * mm});
            skPoint(sketch, "E14.middle", {"position": v(-4.49, 225.94) * mm});
            skLineSegment(sketch, "E15.bottom", {"start": v(-5.28, -391.6) * mm, "end": v(-3.7, -391.6) * mm});
            skLineSegment(sketch, "E15.top", {"start": v(-5.28, -372.54) * mm, "end": v(-3.7, -372.54) * mm});
            skLineSegment(sketch, "E15.left", {"start": v(-5.28, -391.6) * mm, "end": v(-5.28, -372.54) * mm});
            skLineSegment(sketch, "E15.right", {"start": v(-3.7, -391.6) * mm, "end": v(-3.7, -372.54) * mm});
            skPoint(sketch, "E15.middle", {"position": v(-4.49, -382.07) * mm});
            skLineSegment(sketch, "E16.bottom", {"start": v(-5.28, -843.48) * mm, "end": v(-3.7, -843.48) * mm});
            skLineSegment(sketch, "E16.top", {"start": v(-5.28, -824.43) * mm, "end": v(-3.7, -824.43) * mm});
            skLineSegment(sketch, "E16.left", {"start": v(-5.28, -843.48) * mm, "end": v(-5.28, -824.43) * mm});
            skLineSegment(sketch, "E16.right", {"start": v(-3.7, -843.48) * mm, "end": v(-3.7, -824.43) * mm});
            skPoint(sketch, "E16.middle", {"position": v(-4.49, -833.96) * mm});
            skSolve(sketch);
        }
        {
            var Q0;
            Q0 = qSketchRegion(id + "F7", true);
            var Q1;
            Q1=sQuery(id+"F7.wireOp",EDGE,"E12");
            revolve(context, id + "F8", {"operationType" : NewBodyOperationType.ADD, "entities" : qUnion([Q0]), "axis" : qUnion([Q1]), "revolveType" : RevolveType.FULL});
        }
    });
